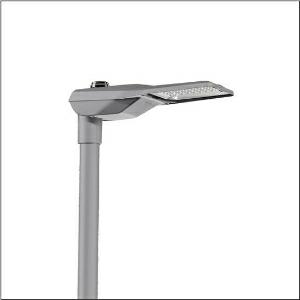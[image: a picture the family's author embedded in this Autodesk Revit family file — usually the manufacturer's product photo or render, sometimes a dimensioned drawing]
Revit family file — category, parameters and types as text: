
# Revit family: streetlight_sl_21_mini___st1_5a_5xe6p47n08hb_ac47
name_source: partatom
category: Lighting Fixtures
units: mm (PartAtom-declared; Revit-internal decimal feet)

## family parameters
Cut with Voids When Loaded = No
Host = Face
Light Source = No
Part Type = Normal
Room Calculation Point = No
Round Connector Dimension = Use Diameter
Shared = No

## types (1)
- --- (1 x LED, 9260 lm, 66 W, 4000K)
    Apparent Load = 66 VA
    CIE Flux Codes = 22 53 95 100 100
    Color Rendering = 70
    Color Temperature = 4000K
    Default Elevation = 1800 mm
    Description = Streetlight SL 21 mini, mast luminaire, primary light control with lens, of PMMA, primary optical cover: cover, of toughened safety glass, transparent, light distribution: ST1.5a, light emission: direct distribution, primary light characteristic: asymmetric, installation type: side-entry, LED, 3G 1.5mm², High Power LED, rated luminous flux: 9.260lm, luminous efficacy: 140lm/W, light colour: 740, colour temperature: 4000K, control gear: NEMA (7pin), control: overheat protection, pre-setting: linear dimming characteristic, constant luminous flux control, time-dependent luminous flux control, flexible luminous flux parameterisation, mains connection: 230..240V, AC, 50/60Hz, connection cable pre-assembled, cable length: 8,5m, wiring characteristics: H07RN-F, start of lifetime: 66W, end of service life: 69W, reduction: 30W, luminaire housing, of diecast aluminium (EN AC-44300), powder-coated, SITECO metallic grey (DB 702S), corrosivity category C5 high according to DIN EN ISO 12944, multi-level sealing system, sealing non-destructively replaceable, inclination adjustable: 0°, 5°, 10°, 15°, length: 628mm, width: 235mm, height: 110mm, spigot size: 42mm (side-entry), mounting height: 4..8m, protection rating (complete): IP66, insulation class (complete): insulation class I (protective earthing), certification: CE, ENEC, ENEC+, VDE, impact resistance: IK10, permissible operating ambient temperature for outdoor applications: -40..+50°C, standard-compliant lighting for roads and squares, packaging unit: 1 piece

Light Distribution: ST1.5a
    Height = 110 mm
    Lamp = 1 x LED
    Lamp Light Flux = 9260 lm
    Lamp Power = 66 W
    Lamp count = 1
    Length = 625 mm
    Luminous efficacy = 140 lm/W
    Manufacturer = Siteco
    ModVariant = No
    Model = 5XE6P47N08HB
    Number of Poles = 1
    OnlyDefault = Yes
    Power Factor = 1
    Product Name = Streetlight SL 21 mini | ST1.5a
    Product group = mast luminaire | pylon top
    ProductGroupID = 6100
    Protection Class = Protection class I
    Protection Degree = IP 66
    RLX_Detail_Level = 1
    RLX_Emergency_Light_Flux = 0 lm
    RLX_Emergency_Type = 0
    RLX_Emergency_Type_DB = No
    RlxData = <blob elided: 29625 chars, md5=476d7e39>
    Socket = socket
    Standby Power = 0 W
    System Light Flux = 9260 lm
    System Power = 66 W
    Type Comments = factory setting: luminous flux: 100 % | dim-lin: 254 | 670 mA
    Type Image = l_1294379.jpg
    URL = http://relux.com
    VarID = @adj_133035
    Voltage = 0 V
    Weight = 0.00 kg
    Width = 234 mm

## geometry (parser evidence)
native form markers: Blend x4, Sweep x9
no freeform markers — native parametric forms only
